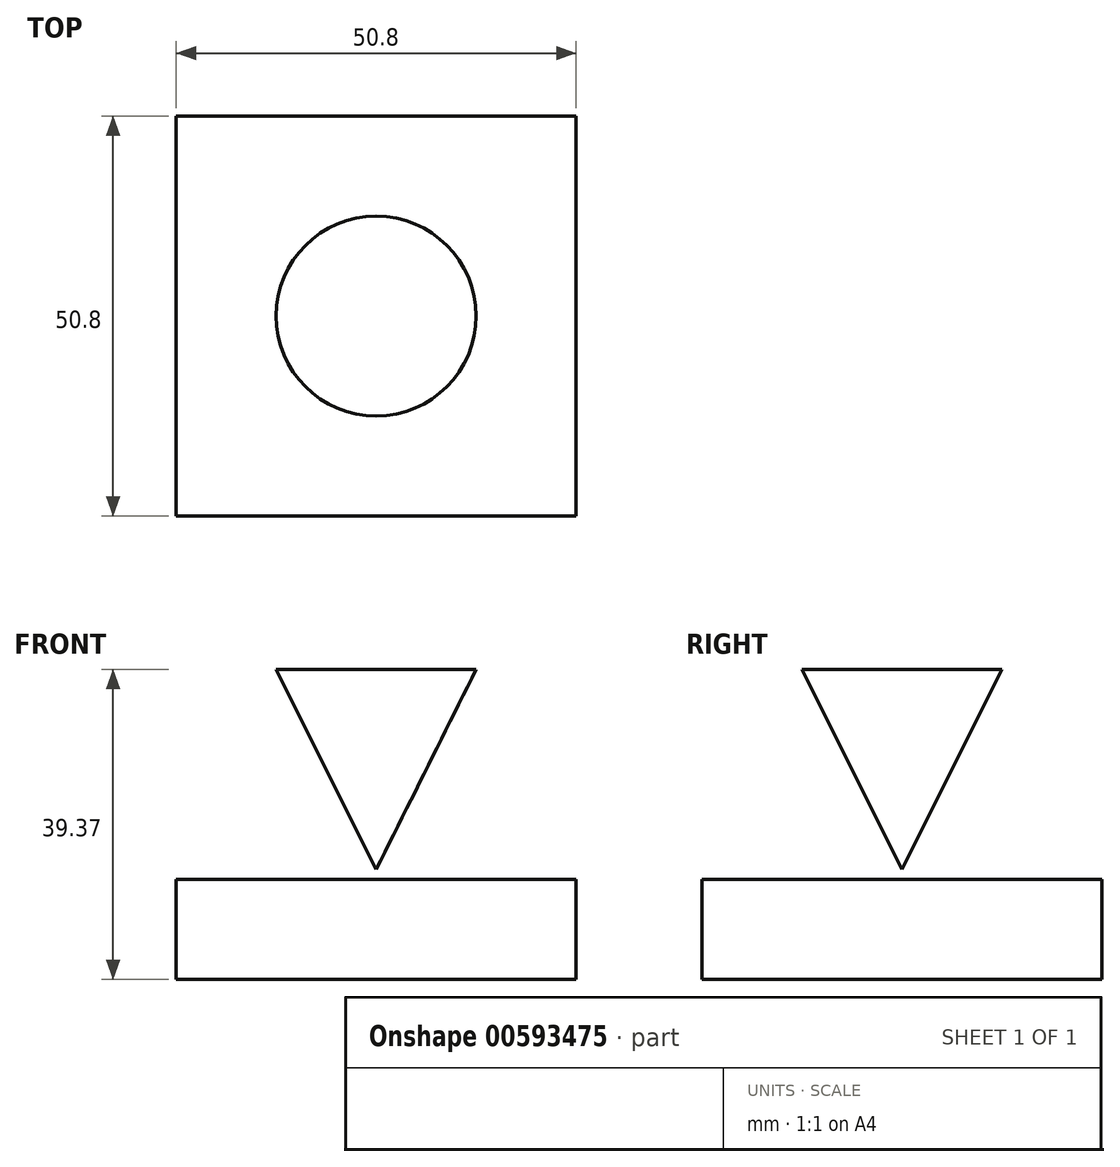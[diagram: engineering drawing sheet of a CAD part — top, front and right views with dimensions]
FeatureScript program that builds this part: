
annotation { "Feature Type Name" : "Feature", "Feature Type Description" : "" }
export const myFeature = defineFeature(function(context is Context, id is Id, definition is map)
    precondition{}
    {
        {
            var Q0;
            Q0=qCreatedBy(makeId("Front.planeOp"),FACE);
            var sketch = newSketch(context, id + "F0", { "sketchPlane" : qUnion([Q0])});
            skLineSegment(sketch, "E0.bottom", {"start": v(25.4, 6.35) * mm, "end": v(-25.4, 6.35) * mm});
            skLineSegment(sketch, "E0.top", {"start": v(25.4, -6.35) * mm, "end": v(-25.4, -6.35) * mm});
            skLineSegment(sketch, "E0.left", {"start": v(25.4, 6.35) * mm, "end": v(25.4, -6.35) * mm});
            skLineSegment(sketch, "E0.right", {"start": v(-25.4, 6.35) * mm, "end": v(-25.4, -6.35) * mm});
            skPoint(sketch, "E0.middle", {"position": v(0, 0) * mm});
            skSolve(sketch);
        }
        {
            var Q0;
            Q0=makeQuery(id+"F0.imprint","IMPRINT",FACE,{"disambiguationData":[TD([[makeQuery(id+"F0.imprint","IMPRINT",EDGE,{"derivedFrom":sQuery(id+"F0.wireOp",EDGE,"E0.bottom")}),1.0]])]});
            extrude(context, id + "F1", {"entities" : qUnion([Q0]), "endBound" : BoundingType.SYMMETRIC, "depth" : 50.8 * mm, "offsetDistance" : 25.4 * mm});
        }
        {
            var Q0;
            Q0=qCreatedBy(makeId("Front.planeOp"),FACE);
            var sketch = newSketch(context, id + "F2", { "sketchPlane" : qUnion([Q0])});
            skLineSegment(sketch, "E1", {"start": v(0, 7.62) * mm, "end": v(12.7, 33.02) * mm});
            skLineSegment(sketch, "E2", {"start": v(12.7, 33.02) * mm, "end": v(0, 33.02) * mm});
            skLineSegment(sketch, "E3", {"start": v(0, 33.02) * mm, "end": v(0, 7.62) * mm});
            skSolve(sketch);
        }
        {
            var Q0;
            Q0=makeQuery(id+"F2.imprint","IMPRINT",FACE,{"disambiguationData":[TD([[makeQuery(id+"F2.imprint","IMPRINT",EDGE,{"derivedFrom":sQuery(id+"F2.wireOp",EDGE,"E1")}),1.0]])]});
            var Q1;
            Q1=sQuery(id+"F2.wireOp",EDGE,"E3");
            revolve(context, id + "F3", {"entities" : qUnion([Q0]), "axis" : qUnion([Q1]), "revolveType" : RevolveType.FULL});
        }
    });
